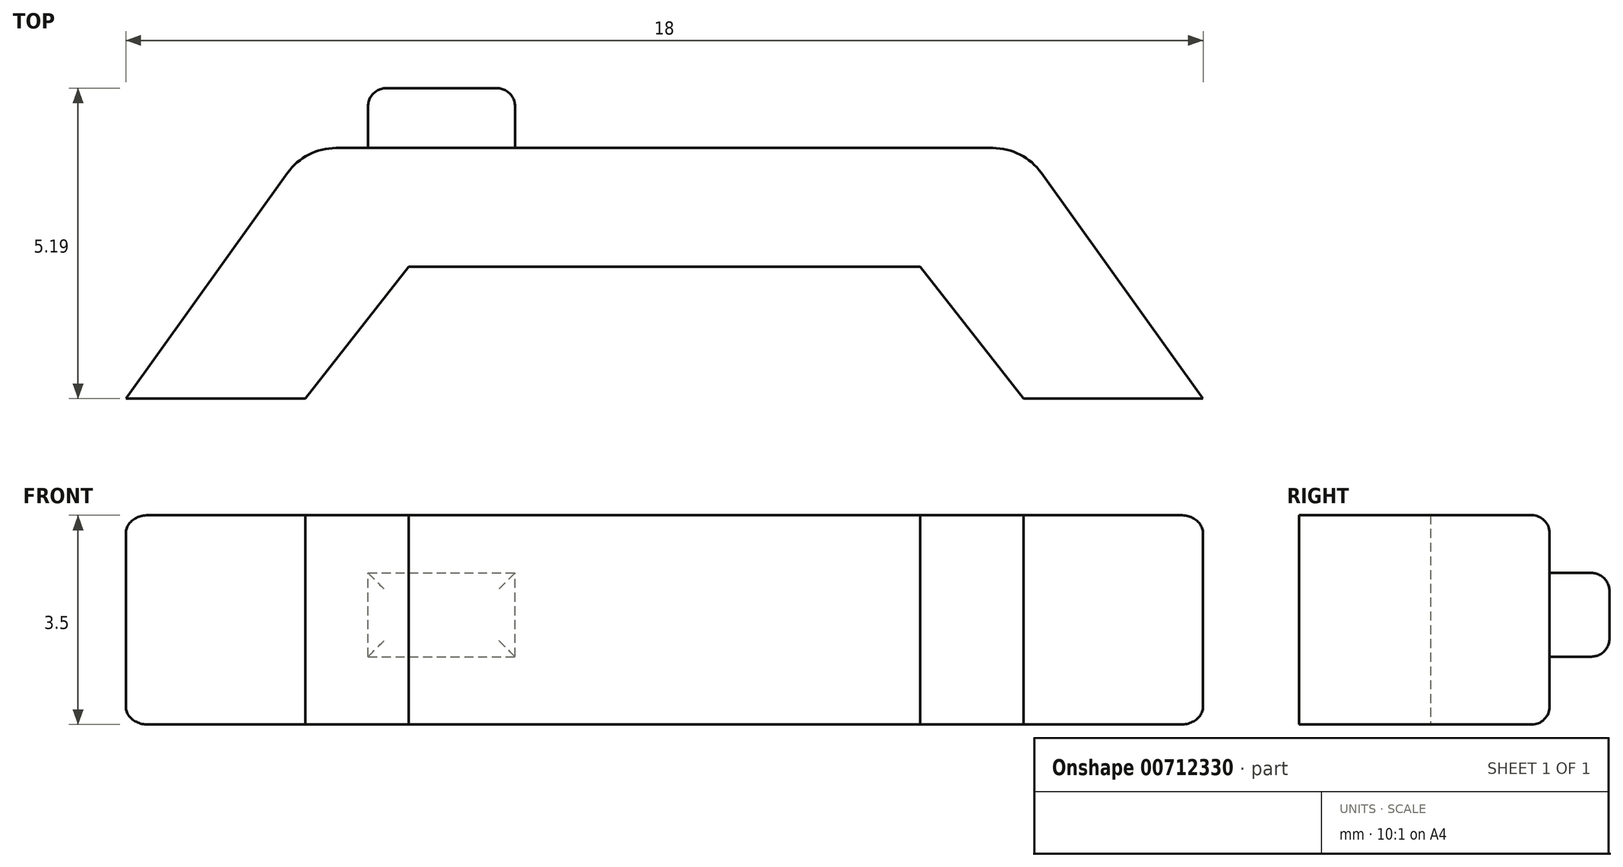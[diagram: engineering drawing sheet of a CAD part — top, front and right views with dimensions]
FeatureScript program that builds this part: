
annotation { "Feature Type Name" : "Feature", "Feature Type Description" : "" }
export const myFeature = defineFeature(function(context is Context, id is Id, definition is map)
    precondition{}
    {
        {
            var Q0;
            Q0=qCreatedBy(makeId("Top.planeOp"),FACE);
            var sketch = newSketch(context, id + "F0", { "sketchPlane" : qUnion([Q0])});
            skLineSegment(sketch, "E0", {"start": v(-14.2, 26.34) * mm, "end": v(-6.5, 26.34) * mm});
            skLineSegment(sketch, "E1", {"start": v(-6.5, 26.34) * mm, "end": v(-6.5, 17.61) * mm, "construction": true});
            skLineSegment(sketch, "E2.MirrorCS", {"start": v(1.19, 26.34) * mm, "end": v(-6.5, 26.34) * mm});
            skLineSegment(sketch, "E3.MirrorCS", {"start": v(2.5, 24.63) * mm, "end": v(1.19, 26.34) * mm});
            skPoint(sketch, "E4.start.orphan", {"position": v(-15.5, 24.63) * mm});
            skLineSegment(sketch, "E5", {"start": v(4.56, 43.39) * mm, "end": v(7.56, 43.39) * mm});
            skLineSegment(sketch, "E6", {"start": v(7.56, 43.39) * mm, "end": v(9.28, 45.6) * mm});
            skLineSegment(sketch, "E7", {"start": v(9.28, 45.6) * mm, "end": v(13.56, 45.6) * mm});
            skLineSegment(sketch, "E8", {"start": v(4.56, 43.39) * mm, "end": v(7.56, 47.58) * mm});
            skLineSegment(sketch, "E9", {"start": v(7.56, 47.58) * mm, "end": v(13.56, 47.58) * mm});
            skLineSegment(sketch, "E10", {"start": v(13.56, 45.6) * mm, "end": v(13.56, 64.23) * mm, "construction": true});
            skLineSegment(sketch, "E11.MirrorCS", {"start": v(17.83, 45.6) * mm, "end": v(13.56, 45.6) * mm});
            skLineSegment(sketch, "E12.MirrorCS", {"start": v(19.56, 47.58) * mm, "end": v(13.56, 47.58) * mm});
            skLineSegment(sketch, "E13.MirrorCS", {"start": v(19.56, 43.39) * mm, "end": v(17.83, 45.6) * mm});
            skLineSegment(sketch, "E14.MirrorCS", {"start": v(22.56, 43.39) * mm, "end": v(19.56, 47.58) * mm});
            skLineSegment(sketch, "E15.MirrorCS", {"start": v(22.56, 43.39) * mm, "end": v(19.56, 43.39) * mm});
            skSolve(sketch);
        }
        {
            var Q0;
            Q0=makeQuery(id+"F0.imprint","IMPRINT",FACE,{"disambiguationData":[TD([[makeQuery(id+"F0.imprint","IMPRINT",EDGE,{"derivedFrom":sQuery(id+"F0.wireOp",EDGE,"E5")}),1.0]])]});
            extrude(context, id + "F1", {"entities" : qUnion([Q0]), "depth" : 3.5 * mm, "offsetDistance" : 25 * mm});
        }
        {
            var Q0;
            Q0=makeQuery(id+"F1.opExtrude","SWEPT_FACE",FACE,{"disambiguationData":[OSD([sQuery(id+"F0.wireOp",EDGE,"E9"),sQuery(id+"F0.wireOp",EDGE,"E12.MirrorCS")])]});
            var sketch = newSketch(context, id + "F2", { "sketchPlane" : qUnion([Q0])});
            skLineSegment(sketch, "E16.bottom", {"start": v(-8.6, 1.14) * mm, "end": v(-11.06, 1.14) * mm});
            skLineSegment(sketch, "E16.top", {"start": v(-8.6, 2.53) * mm, "end": v(-11.06, 2.53) * mm});
            skLineSegment(sketch, "E16.left", {"start": v(-8.6, 1.14) * mm, "end": v(-8.6, 2.53) * mm});
            skLineSegment(sketch, "E16.right", {"start": v(-11.06, 1.14) * mm, "end": v(-11.06, 2.53) * mm});
            skSolve(sketch);
        }
        {
            var Q0;
            Q0=makeQuery(id+"F2.imprint","IMPRINT",FACE,{"disambiguationData":[TD([[makeQuery(id+"F2.imprint","IMPRINT",EDGE,{"derivedFrom":sQuery(id+"F2.wireOp",EDGE,"E16.bottom")}),-1.0]])]});
            extrude(context, id + "F3", {"entities" : qUnion([Q0]), "operationType" : NewBodyOperationType.ADD, "depth" : 1 * mm, "offsetDistance" : 25 * mm});
        }
        {
            var Q0;
            Q0=makeQuery(id+"F1.opExtrude","SWEPT_EDGE",EDGE,{"disambiguationData":[OSD([sQuery(id+"F0.wireOp",EDGE,"E8"),sQuery(id+"F0.wireOp",EDGE,"E9")])]});
            var Q1;
            Q1=makeQuery(id+"F1.opExtrude","SWEPT_EDGE",EDGE,{"disambiguationData":[OSD([sQuery(id+"F0.wireOp",EDGE,"E12.MirrorCS"),sQuery(id+"F0.wireOp",EDGE,"E14.MirrorCS")])]});
            fillet(context, id + "F4", {"entities" : qUnion([Q0, Q1]), "tangentPropagation" : true, "radius" : 1 * mm, "defaultsChanged" : false, "vertexSettings" : [], "allowEdgeOverflow" : false});
        }
        {
            var Q0;
            Q0=makeQuery(id+"F1.opExtrude","CAP_EDGE",EDGE,{"disambiguationData":[OSD([sQuery(id+"F0.wireOp",EDGE,"E8")])],"isStart":false});
            var Q1;
            Q1=makeQuery(id+"F1.opExtrude","CAP_EDGE",EDGE,{"disambiguationData":[OSD([sQuery(id+"F0.wireOp",EDGE,"E9"),sQuery(id+"F0.wireOp",EDGE,"E12.MirrorCS")])],"isStart":true});
            var Q2;
            Q2=makeQuery(id+"F3.opExtrude","CAP_EDGE",EDGE,{"disambiguationData":[OSD([sQuery(id+"F2.wireOp",EDGE,"E16.top")])],"isStart":false});
            var Q3;
            Q3=makeQuery(id+"F3.opExtrude","CAP_EDGE",EDGE,{"disambiguationData":[OSD([sQuery(id+"F2.wireOp",EDGE,"E16.right")])],"isStart":false});
            var Q4;
            Q4=makeQuery(id+"F3.opExtrude","CAP_EDGE",EDGE,{"disambiguationData":[OSD([sQuery(id+"F2.wireOp",EDGE,"E16.left")])],"isStart":false});
            var Q5;
            Q5=makeQuery(id+"F3.opExtrude","CAP_EDGE",EDGE,{"disambiguationData":[OSD([sQuery(id+"F2.wireOp",EDGE,"E16.bottom")])],"isStart":false});
            fillet(context, id + "F5", {"entities" : qUnion([Q0, Q1, Q2, Q3, Q4, Q5]), "tangentPropagation" : true, "radius" : .3 * mm, "defaultsChanged" : false, "vertexSettings" : [], "allowEdgeOverflow" : false});
        }
    });
